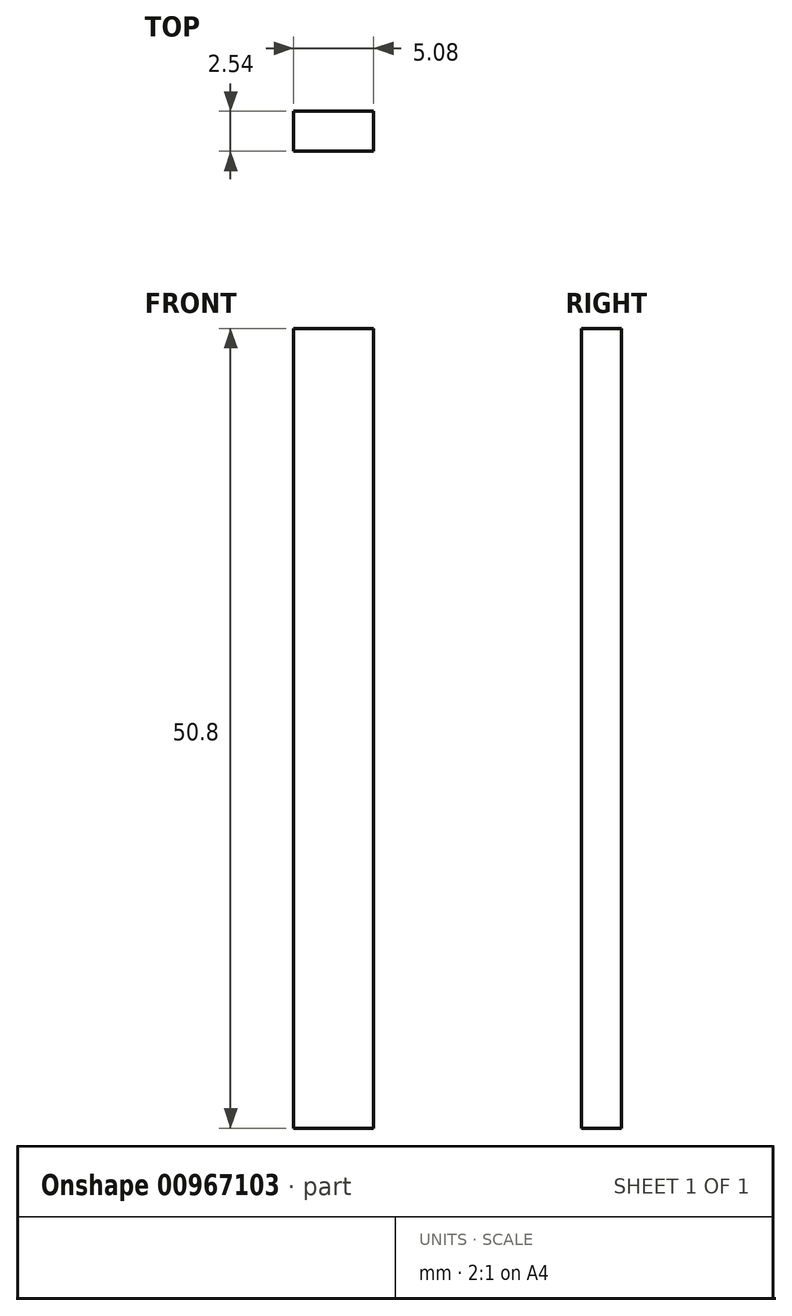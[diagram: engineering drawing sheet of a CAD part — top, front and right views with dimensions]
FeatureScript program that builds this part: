
annotation { "Feature Type Name" : "Feature", "Feature Type Description" : "" }
export const myFeature = defineFeature(function(context is Context, id is Id, definition is map)
    precondition{}
    {
        {
            var Q0;
            Q0=qCreatedBy(makeId("Front.planeOp"),FACE);
            var sketch = newSketch(context, id + "F0", { "sketchPlane" : qUnion([Q0])});
            skLineSegment(sketch, "E0.bottom", {"start": v(0, 0) * mm, "end": v(5.08, 0) * mm});
            skLineSegment(sketch, "E0.top", {"start": v(0, 50.8) * mm, "end": v(5.08, 50.8) * mm});
            skLineSegment(sketch, "E0.left", {"start": v(0, 0) * mm, "end": v(0, 50.8) * mm});
            skLineSegment(sketch, "E0.right", {"start": v(5.08, 0) * mm, "end": v(5.08, 50.8) * mm});
            skSolve(sketch);
        }
        {
            var Q0;
            Q0=makeQuery(id+"F0.imprint","IMPRINT",FACE,{"disambiguationData":[TD([[makeQuery(id+"F0.imprint","IMPRINT",EDGE,{"derivedFrom":sQuery(id+"F0.wireOp",EDGE,"E0.bottom")}),1.0]])]});
            extrude(context, id + "F1", {"entities" : qUnion([Q0]), "depth" : 2.54 * mm, "offsetDistance" : 25.4 * mm});
        }
    });
